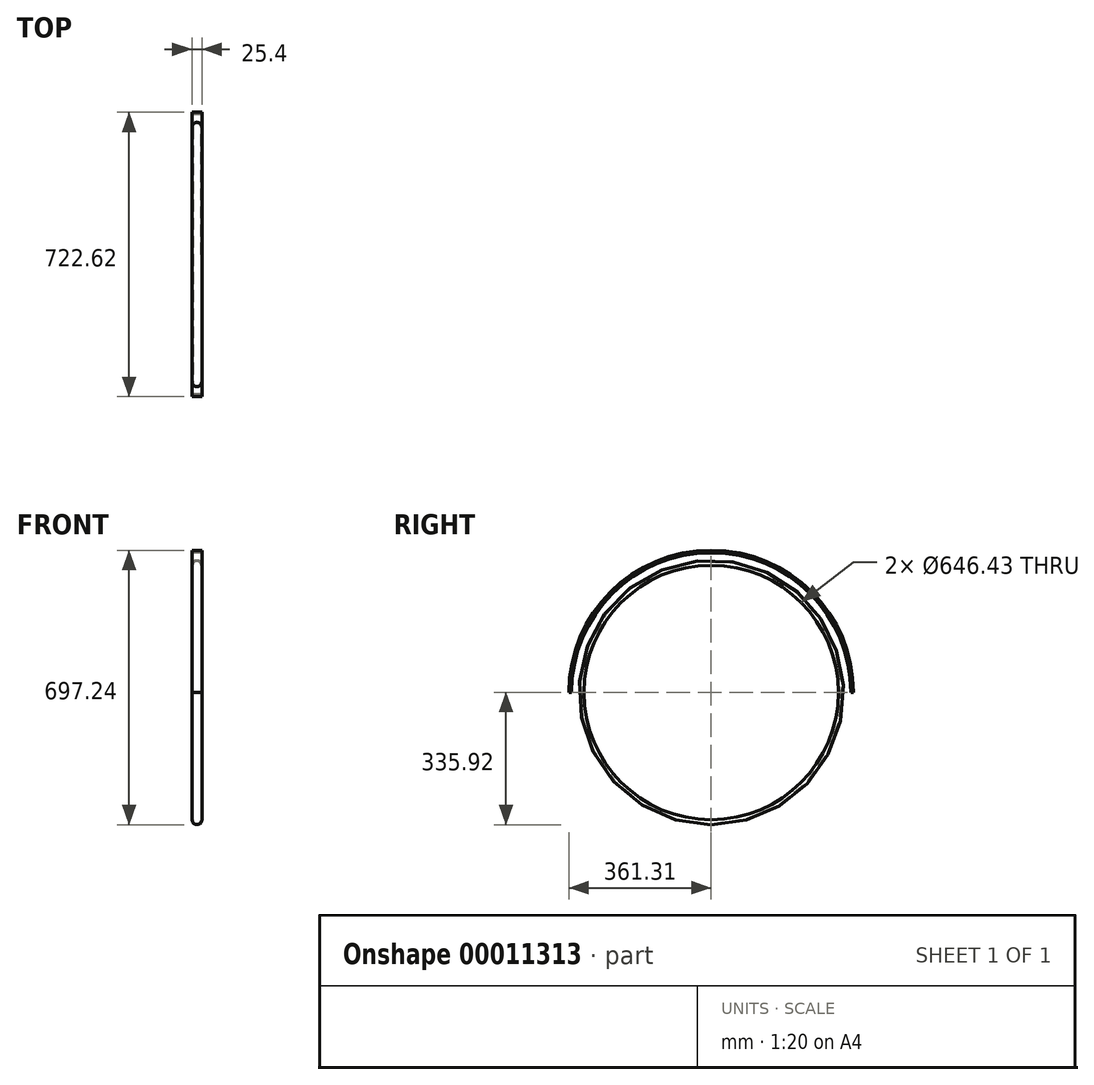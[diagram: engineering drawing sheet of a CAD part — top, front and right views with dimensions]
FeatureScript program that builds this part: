
annotation { "Feature Type Name" : "Feature", "Feature Type Description" : "" }
export const myFeature = defineFeature(function(context is Context, id is Id, definition is map)
    precondition{}
    {
        {
            var Q0;
            Q0=qCreatedBy(makeId("Right.planeOp"),FACE);
            var sketch = newSketch(context, id + "F0", { "sketchPlane" : qUnion([Q0])});
            skCircle(sketch, "E0", {"center": v(0, 0) * mm, "radius": 335.92 * mm});
            skArc(sketch, "E1", {"start": v(354.97, 0) * mm, "mid": v(0, 354.97) * mm, "end": v(-354.97, 0) * mm});
            skArc(sketch, "E2.0", {"start": v(361.32, 0) * mm, "mid": v(0, 361.32) * mm, "end": v(-361.32, 0) * mm});
            skLineSegment(sketch, "E3", {"start": v(-361.32, 0) * mm, "end": v(-354.97, 0) * mm});
            skLineSegment(sketch, "E4", {"start": v(354.97, 0) * mm, "end": v(361.32, 0) * mm});
            skSolve(sketch);
        }
        {
            var Q0;
            Q0 = qSketchRegion(id + "F0", true);
            extrude(context, id + "F1", {"entities" : qUnion([Q0]), "endBound" : BoundingType.SYMMETRIC, "depth" : 25.4 * mm});
        }
        {
            var Q0;
            Q0=makeQuery(id+"F1.opExtrude","CAP_EDGE",EDGE,{"disambiguationData":[OSD([sQuery(id+"F0.wireOp",EDGE,"E0")])],"isStart":false});
            var Q1;
            Q1=makeQuery(id+"F1.opExtrude","CAP_EDGE",EDGE,{"disambiguationData":[OSD([sQuery(id+"F0.wireOp",EDGE,"E0")])],"isStart":true});
            fillet(context, id + "F2", {"entities" : qUnion([Q0, Q1]), "radius" : 12.7 * mm, "tangentPropagation" : true, "allowEdgeOverflow" : false});
        }
        {
            var Q0;
            Q0=makeQuery(id+"F1.opExtrude","CAP_FACE",FACE,{"disambiguationData":[OSD([sQuery(id+"F0.wireOp",EDGE,"E0")])],"isStart":false});
            var Q1;
            Q1=makeQuery(id+"F1.opExtrude","CAP_FACE",FACE,{"disambiguationData":[OSD([sQuery(id+"F0.wireOp",EDGE,"E0")])],"isStart":true});
            shell(context, id + "F3", {"entities" : qUnion([Q0, Q1]), "thickness" : 2.54 * mm});
        }
    });
